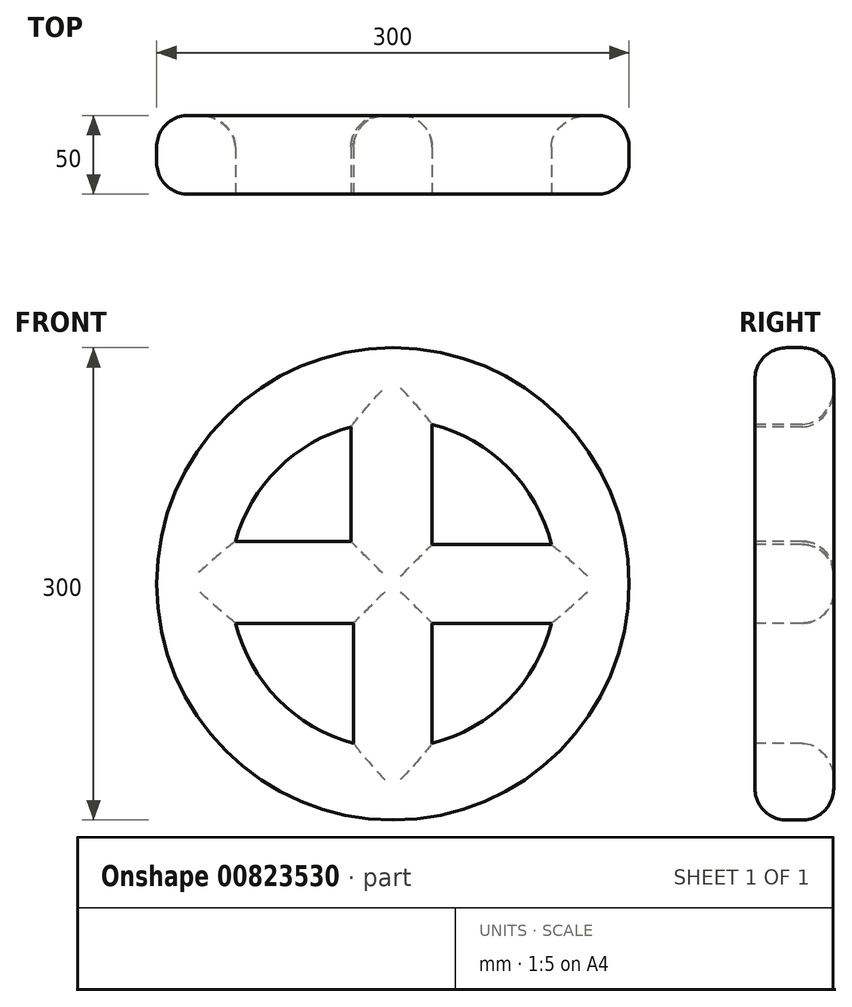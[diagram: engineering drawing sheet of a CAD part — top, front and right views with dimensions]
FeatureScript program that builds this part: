
annotation { "Feature Type Name" : "Feature", "Feature Type Description" : "" }
export const myFeature = defineFeature(function(context is Context, id is Id, definition is map)
    precondition{}
    {
        {
            var Q0;
            Q0=qCreatedBy(makeId("Front.planeOp"),FACE);
            var sketch = newSketch(context, id + "F0", { "sketchPlane" : qUnion([Q0])});
            skCircle(sketch, "E0", {"center": v(0, 0) * mm, "radius": 150 * mm});
            skSolve(sketch);
        }
        {
            var Q0;
            Q0 = qSketchRegion(id + "F0", true);
            extrude(context, id + "F1", {"entities" : qUnion([Q0]), "depth" : 50 * mm, "offsetDistance" : 25 * mm});
        }
        {
            var Q0;
            Q0=makeQuery(id+"F1.opExtrude","CAP_FACE",FACE,{"disambiguationData":[OSD([sQuery(id+"F0.wireOp",EDGE,"E0")])],"isStart":false});
            var sketch = newSketch(context, id + "F2", { "sketchPlane" : qUnion([Q0])});
            skPoint(sketch, "E1", {"position": v(0, -150) * mm});
            skPoint(sketch, "E2", {"position": v(150, 0) * mm});
            skPoint(sketch, "E3", {"position": v(0, 150) * mm});
            skPoint(sketch, "E4", {"position": v(-150, 0) * mm});
            skPoint(sketch, "E5", {"position": v(-50, 0) * mm});
            skPoint(sketch, "E6", {"position": v(0, -50) * mm});
            skPoint(sketch, "E7", {"position": v(50, 0) * mm});
            skPoint(sketch, "E8", {"position": v(0, 50) * mm});
            skSolve(sketch);
        }
        {
            var Q0;
            Q0=makeQuery(id+"F2.imprint","IMPRINT",FACE,{"disambiguationData":[TD([[makeQuery(id+"F2.imprint","IMPRINT",EDGE,{"derivedFrom":makeQuery(id+"F1.opExtrude","CAP_EDGE",EDGE,{"disambiguationData":[OSD([sQuery(id+"F0.wireOp",EDGE,"E0")])],"isStart":false})}),1.0]])]});
            var sketch = newSketch(context, id + "F3", { "sketchPlane" : qUnion([Q0])});
            skPoint(sketch, "E9", {"position": v(-99.93, 0) * mm});
            skPoint(sketch, "E10", {"position": v(0, 99.39) * mm});
            skPoint(sketch, "E11", {"position": v(99.72, 0) * mm});
            skPoint(sketch, "E12", {"position": v(0, -100.26) * mm});
            skSolve(sketch);
        }
        {
            var Q0;
            Q0=makeQuery(id+"F3.imprint","IMPRINT",FACE,{"disambiguationData":[TD([[makeQuery(id+"F3.imprint","IMPRINT",EDGE,{"derivedFrom":makeQuery(id+"F2.imprint","IMPRINT",EDGE,{"derivedFrom":makeQuery(id+"F1.opExtrude","CAP_EDGE",EDGE,{"disambiguationData":[OSD([sQuery(id+"F0.wireOp",EDGE,"E0")])],"isStart":false})})}),1.0]])]});
            var sketch = newSketch(context, id + "F4", { "sketchPlane" : qUnion([Q0])});
            skLineSegment(sketch, "E13", {"start": v(-100, 26.98) * mm, "end": v(-26.68, 26.98) * mm});
            skLineSegment(sketch, "E14", {"start": v(-26.68, 26.98) * mm, "end": v(-26.68, 99.7) * mm});
            skLineSegment(sketch, "E15", {"start": v(-99.8, -25) * mm, "end": v(-25, -25) * mm});
            skLineSegment(sketch, "E16", {"start": v(-25, -25) * mm, "end": v(-25, -101.27) * mm});
            skArc(sketch, "E17", {"start": v(-99.8, -25) * mm, "mid": v(-72.94, -73.47) * mm, "end": v(-25, -101.27) * mm});
            skLineSegment(sketch, "E18", {"start": v(25, 101.37) * mm, "end": v(25, 25) * mm});
            skLineSegment(sketch, "E19", {"start": v(25, 25) * mm, "end": v(100.66, 25) * mm});
            skArc(sketch, "E20", {"start": v(100.66, 25) * mm, "mid": v(73.46, 73.72) * mm, "end": v(25, 101.37) * mm});
            skLineSegment(sketch, "E21", {"start": v(25, -101.27) * mm, "end": v(25, -25) * mm});
            skLineSegment(sketch, "E22", {"start": v(25, -25) * mm, "end": v(100.66, -25) * mm});
            skArc(sketch, "E23", {"start": v(25, -101.27) * mm, "mid": v(73.44, -73.66) * mm, "end": v(100.66, -25) * mm});
            skArc(sketch, "E24", {"start": v(-26.68, 99.7) * mm, "mid": v(-73, 73.09) * mm, "end": v(-100, 26.98) * mm});
            skSolve(sketch);
        }
        {
            var Q0;
            Q0 = qSketchRegion(id + "F4", true);
            extrude(context, id + "F5", {"entities" : qUnion([Q0]), "operationType" : NewBodyOperationType.REMOVE, "oppositeDirection" : true, "depth" : 102 * mm, "offsetDistance" : 25 * mm});
        }
        {
            var Q0;
            Q0=makeQuery(id+"F1.opExtrude","CAP_EDGE",EDGE,{"disambiguationData":[OSD([sQuery(id+"F0.wireOp",EDGE,"E0")])],"isStart":true});
            var Q1;
            Q1=makeQuery(id+"F1.opExtrude","CAP_EDGE",EDGE,{"disambiguationData":[OSD([sQuery(id+"F0.wireOp",EDGE,"E0")])],"isStart":false});
            fillet(context, id + "F6", {"entities" : qUnion([Q0, Q1]), "radius" : 20 * mm, "tangentPropagation" : true, "allowEdgeOverflow" : false});
        }
        {
            var Q0;
            Q0=makeQuery(id+"F5.boolean.opBoolean","INTERSECT",EDGE,{"derivedFrom":[makeQuery(id+"F1.opExtrude","CAP_FACE",FACE,{"disambiguationData":[OSD([sQuery(id+"F0.wireOp",EDGE,"E0")])],"isStart":true}),makeQuery(id+"F5.opExtrude","SWEPT_FACE",FACE,{"disambiguationData":[OSD([sQuery(id+"F4.wireOp",EDGE,"E19")])]})]});
            var Q1;
            Q1=makeQuery(id+"F5.boolean.opBoolean","INTERSECT",EDGE,{"derivedFrom":[makeQuery(id+"F1.opExtrude","CAP_FACE",FACE,{"disambiguationData":[OSD([sQuery(id+"F0.wireOp",EDGE,"E0")])],"isStart":true}),makeQuery(id+"F5.opExtrude","SWEPT_FACE",FACE,{"disambiguationData":[OSD([sQuery(id+"F4.wireOp",EDGE,"E18")])]})]});
            var Q2;
            Q2=makeQuery(id+"F5.boolean.opBoolean","INTERSECT",EDGE,{"derivedFrom":[makeQuery(id+"F1.opExtrude","CAP_FACE",FACE,{"disambiguationData":[OSD([sQuery(id+"F0.wireOp",EDGE,"E0")])],"isStart":true}),makeQuery(id+"F5.opExtrude","SWEPT_FACE",FACE,{"disambiguationData":[OSD([sQuery(id+"F4.wireOp",EDGE,"E20")])]})]});
            var Q3;
            Q3=makeQuery(id+"F5.boolean.opBoolean","INTERSECT",EDGE,{"derivedFrom":[makeQuery(id+"F1.opExtrude","CAP_FACE",FACE,{"disambiguationData":[OSD([sQuery(id+"F0.wireOp",EDGE,"E0")])],"isStart":true}),makeQuery(id+"F5.opExtrude","SWEPT_FACE",FACE,{"disambiguationData":[OSD([sQuery(id+"F4.wireOp",EDGE,"E24")])]})]});
            var Q4;
            Q4=makeQuery(id+"F5.boolean.opBoolean","INTERSECT",EDGE,{"derivedFrom":[makeQuery(id+"F1.opExtrude","CAP_FACE",FACE,{"disambiguationData":[OSD([sQuery(id+"F0.wireOp",EDGE,"E0")])],"isStart":true}),makeQuery(id+"F5.opExtrude","SWEPT_FACE",FACE,{"disambiguationData":[OSD([sQuery(id+"F4.wireOp",EDGE,"E13")])]})]});
            var Q5;
            Q5=makeQuery(id+"F5.boolean.opBoolean","INTERSECT",EDGE,{"derivedFrom":[makeQuery(id+"F1.opExtrude","CAP_FACE",FACE,{"disambiguationData":[OSD([sQuery(id+"F0.wireOp",EDGE,"E0")])],"isStart":true}),makeQuery(id+"F5.opExtrude","SWEPT_FACE",FACE,{"disambiguationData":[OSD([sQuery(id+"F4.wireOp",EDGE,"E14")])]})]});
            var Q6;
            Q6=makeQuery(id+"F5.boolean.opBoolean","INTERSECT",EDGE,{"derivedFrom":[makeQuery(id+"F1.opExtrude","CAP_FACE",FACE,{"disambiguationData":[OSD([sQuery(id+"F0.wireOp",EDGE,"E0")])],"isStart":true}),makeQuery(id+"F5.opExtrude","SWEPT_FACE",FACE,{"disambiguationData":[OSD([sQuery(id+"F4.wireOp",EDGE,"E16")])]})]});
            var Q7;
            Q7=makeQuery(id+"F5.boolean.opBoolean","INTERSECT",EDGE,{"derivedFrom":[makeQuery(id+"F1.opExtrude","CAP_FACE",FACE,{"disambiguationData":[OSD([sQuery(id+"F0.wireOp",EDGE,"E0")])],"isStart":true}),makeQuery(id+"F5.opExtrude","SWEPT_FACE",FACE,{"disambiguationData":[OSD([sQuery(id+"F4.wireOp",EDGE,"E15")])]})]});
            var Q8;
            Q8=makeQuery(id+"F5.boolean.opBoolean","INTERSECT",EDGE,{"derivedFrom":[makeQuery(id+"F1.opExtrude","CAP_FACE",FACE,{"disambiguationData":[OSD([sQuery(id+"F0.wireOp",EDGE,"E0")])],"isStart":true}),makeQuery(id+"F5.opExtrude","SWEPT_FACE",FACE,{"disambiguationData":[OSD([sQuery(id+"F4.wireOp",EDGE,"E17")])]})]});
            var Q9;
            Q9=makeQuery(id+"F5.boolean.opBoolean","INTERSECT",EDGE,{"derivedFrom":[makeQuery(id+"F1.opExtrude","CAP_FACE",FACE,{"disambiguationData":[OSD([sQuery(id+"F0.wireOp",EDGE,"E0")])],"isStart":true}),makeQuery(id+"F5.opExtrude","SWEPT_FACE",FACE,{"disambiguationData":[OSD([sQuery(id+"F4.wireOp",EDGE,"E21")])]})]});
            var Q10;
            Q10=makeQuery(id+"F5.boolean.opBoolean","INTERSECT",EDGE,{"derivedFrom":[makeQuery(id+"F1.opExtrude","CAP_FACE",FACE,{"disambiguationData":[OSD([sQuery(id+"F0.wireOp",EDGE,"E0")])],"isStart":true}),makeQuery(id+"F5.opExtrude","SWEPT_FACE",FACE,{"disambiguationData":[OSD([sQuery(id+"F4.wireOp",EDGE,"E22")])]})]});
            var Q11;
            Q11=makeQuery(id+"F5.boolean.opBoolean","INTERSECT",EDGE,{"derivedFrom":[makeQuery(id+"F1.opExtrude","CAP_FACE",FACE,{"disambiguationData":[OSD([sQuery(id+"F0.wireOp",EDGE,"E0")])],"isStart":true}),makeQuery(id+"F5.opExtrude","SWEPT_FACE",FACE,{"disambiguationData":[OSD([sQuery(id+"F4.wireOp",EDGE,"E23")])]})]});
            fillet(context, id + "F7", {"entities" : qUnion([Q0, Q1, Q2, Q3, Q4, Q5, Q6, Q7, Q8, Q9, Q10, Q11]), "radius" : 20 * mm, "tangentPropagation" : true, "allowEdgeOverflow" : false});
        }
    });
